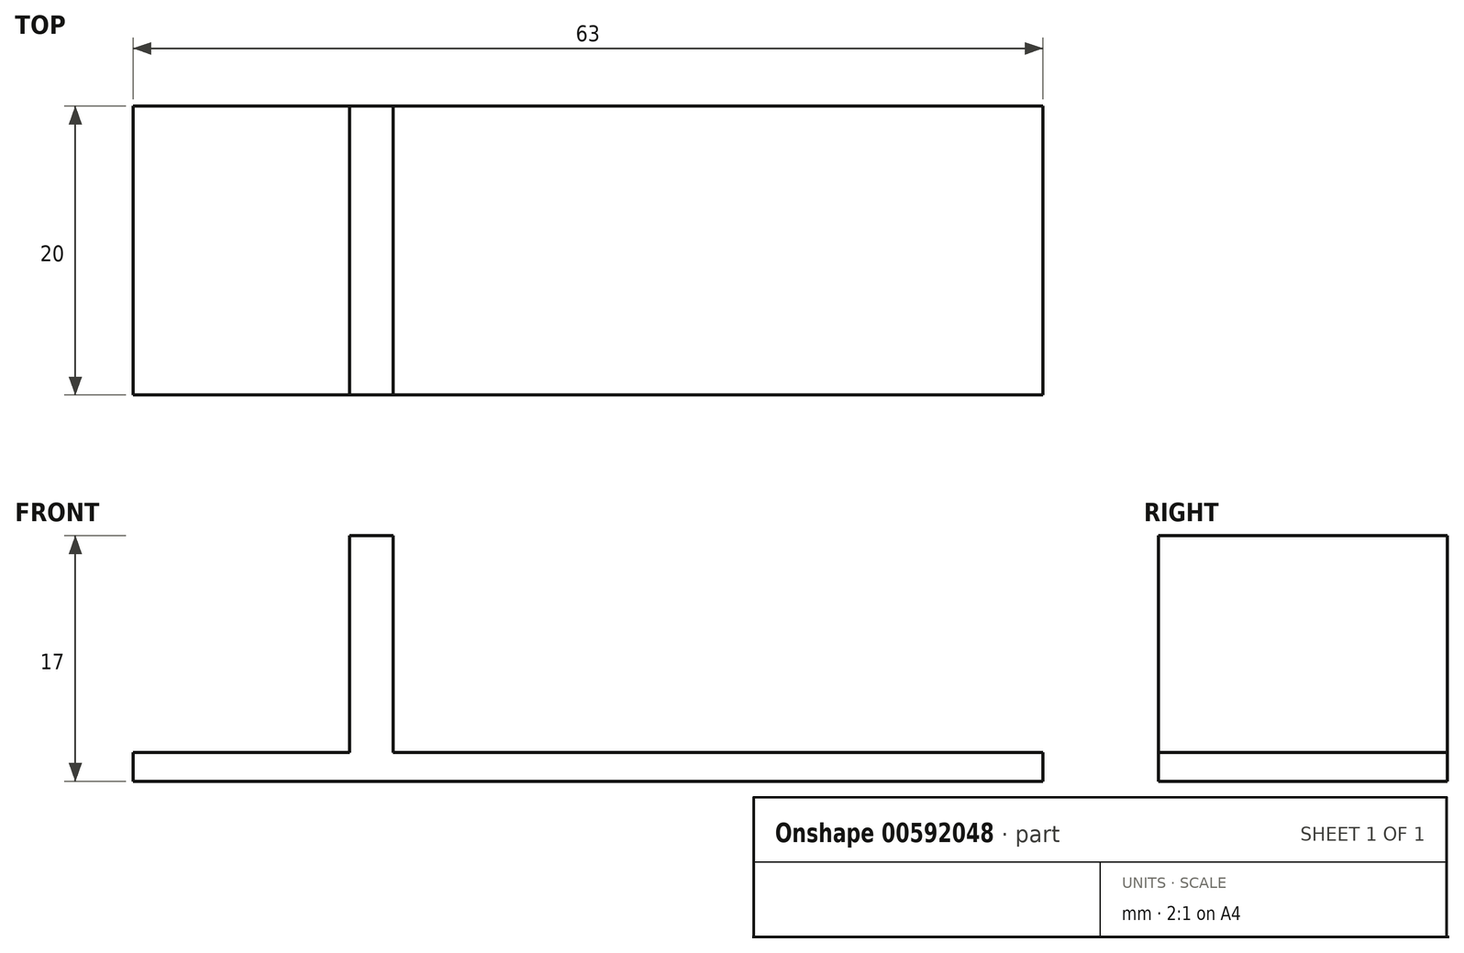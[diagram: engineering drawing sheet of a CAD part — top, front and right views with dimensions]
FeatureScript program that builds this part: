
annotation { "Feature Type Name" : "Feature", "Feature Type Description" : "" }
export const myFeature = defineFeature(function(context is Context, id is Id, definition is map)
    precondition{}
    {
        {
            var Q0;
            Q0=qCreatedBy(makeId("Top.planeOp"),FACE);
            var sketch = newSketch(context, id + "F0", { "sketchPlane" : qUnion([Q0])});
            skLineSegment(sketch, "E0.bottom", {"start": v(-61.65, 31.43) * mm, "end": v(1.35, 31.43) * mm});
            skLineSegment(sketch, "E0.top", {"start": v(-61.65, 11.43) * mm, "end": v(1.35, 11.43) * mm});
            skLineSegment(sketch, "E0.left", {"start": v(-61.65, 31.43) * mm, "end": v(-61.65, 11.43) * mm});
            skLineSegment(sketch, "E0.right", {"start": v(1.35, 31.43) * mm, "end": v(1.35, 11.43) * mm});
            skLineSegment(sketch, "E1", {"start": v(-43.65, 31.43) * mm, "end": v(-43.65, 11.43) * mm});
            skLineSegment(sketch, "E2", {"start": v(-46.65, 31.43) * mm, "end": v(-46.65, 11.43) * mm});
            skSolve(sketch);
        }
        {
            var Q0;
            {var subQ2=sQuery(id+"F0.wireOp",EDGE,"E0.right");Q0=makeQuery(id+"F0.imprint","IMPRINT",FACE,{"disambiguationData":[TD([[makeQuery(id+"F0.imprint","IMPRINT",EDGE,{"derivedFrom":subQ2}),-1.0]])]});}
            var Q1;
            {var subQ0=sQuery(id+"F0.wireOp",EDGE,"E1");Q1=makeQuery(id+"F0.imprint","IMPRINT",FACE,{"disambiguationData":[TD([[makeQuery(id+"F0.imprint","IMPRINT",EDGE,{"derivedFrom":subQ0}),-1.0]])]});}
            var Q2;
            {var subQ0=sQuery(id+"F0.wireOp",EDGE,"E0.left");Q2=makeQuery(id+"F0.imprint","IMPRINT",FACE,{"disambiguationData":[TD([[makeQuery(id+"F0.imprint","IMPRINT",EDGE,{"derivedFrom":subQ0}),1.0]])]});}
            extrude(context, id + "F1", {"entities" : qUnion([Q0, Q1, Q2]), "oppositeDirection" : true, "depth" : 2 * mm, "offsetDistance" : 25 * mm});
        }
        {
            var Q0;
            {var subQ0=sQuery(id+"F0.wireOp",EDGE,"E1");Q0=makeQuery(id+"F0.imprint","IMPRINT",FACE,{"disambiguationData":[TD([[makeQuery(id+"F0.imprint","IMPRINT",EDGE,{"derivedFrom":subQ0}),-1.0]])]});}
            extrude(context, id + "F2", {"entities" : qUnion([Q0]), "operationType" : NewBodyOperationType.ADD, "depth" : 15 * mm, "offsetDistance" : 25 * mm});
        }
    });
